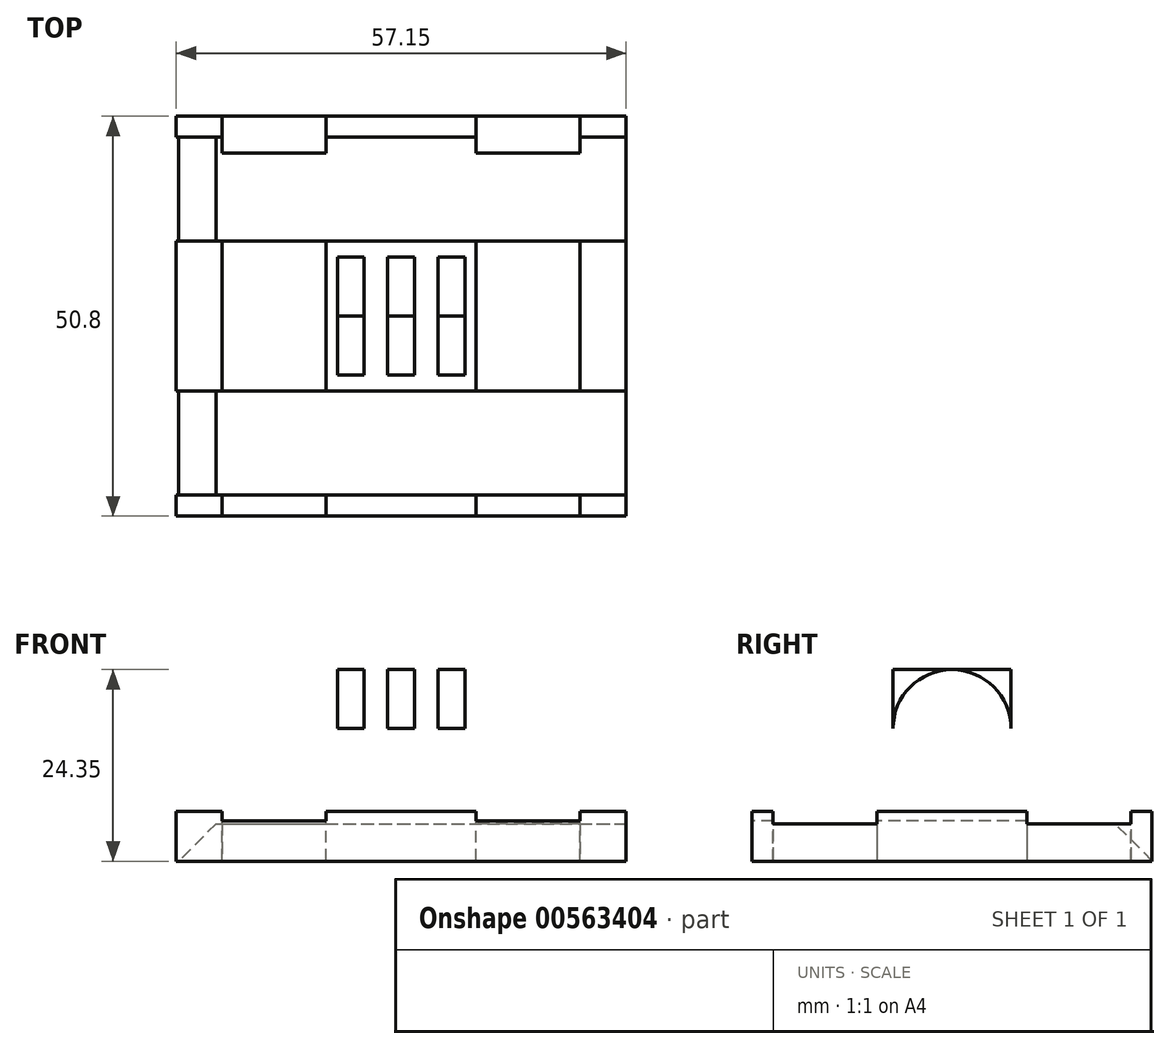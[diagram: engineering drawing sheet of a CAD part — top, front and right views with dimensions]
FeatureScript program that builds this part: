
annotation { "Feature Type Name" : "Feature", "Feature Type Description" : "" }
export const myFeature = defineFeature(function(context is Context, id is Id, definition is map)
    precondition{}
    {
        {
            var Q0;
            Q0=qCreatedBy(makeId("Top.planeOp"),FACE);
            var sketch = newSketch(context, id + "F0", { "sketchPlane" : qUnion([Q0])});
            skLineSegment(sketch, "E0.bottom", {"start": v(-28.58, 25.4) * mm, "end": v(28.58, 25.4) * mm});
            skLineSegment(sketch, "E0.top", {"start": v(-28.58, -25.4) * mm, "end": v(28.58, -25.4) * mm});
            skLineSegment(sketch, "E0.left", {"start": v(-28.57, 25.4) * mm, "end": v(-28.58, -25.4) * mm});
            skLineSegment(sketch, "E0.right", {"start": v(28.58, 25.4) * mm, "end": v(28.57, -25.4) * mm});
            skPoint(sketch, "E0.middle", {"position": v(0, 0) * mm});
            skSolve(sketch);
        }
        {
            var Q0;
            Q0=makeQuery(id+"F0.imprint","IMPRINT",FACE,{"disambiguationData":[TD([[makeQuery(id+"F0.imprint","IMPRINT",EDGE,{"derivedFrom":sQuery(id+"F0.wireOp",EDGE,"E0.bottom")}),-1.0]])]});
            extrude(context, id + "F1", {"entities" : qUnion([Q0]), "depth" : 6.35 * mm, "offsetDistance" : 25.4 * mm});
        }
        {
            var Q0;
            Q0=makeQuery(id+"FtcuCWjjDslHPHS_1.boolean.opBoolean","MERGE",FACE,{"derivedFrom":[makeQuery(id+"F1.opExtrude","SWEPT_FACE",FACE,{"disambiguationData":[OSD([sQuery(id+"F0.wireOp",EDGE,"E0.top")])]}),makeQuery(id+"FtcuCWjjDslHPHS_1.opExtrude","SWEPT_FACE",FACE,{"disambiguationData":[OSD([sQuery(id+"FMVw0hR87RWjdVx_1.wireOp",EDGE,"ffXjeifS-v08F-Zf74-KwMz-o1rhuZgXpIRW.top")])]}),makeQuery(id+"FtcuCWjjDslHPHS_1.opExtrude","SWEPT_FACE",FACE,{"disambiguationData":[OSD([sQuery(id+"FMVw0hR87RWjdVx_1.wireOp",EDGE,"9689fe90-bb07-47c0-8046-fc975a32ab120.MirrorCS")])]})]});
            var sketch = newSketch(context, id + "F2", { "sketchPlane" : qUnion([Q0])});
            skLineSegment(sketch, "E1.bottom", {"start": v(-22.73, 6.35) * mm, "end": v(-9.53, 6.35) * mm});
            skLineSegment(sketch, "E1.top", {"start": v(-22.73, 5.16) * mm, "end": v(-9.53, 5.16) * mm});
            skLineSegment(sketch, "E1.left", {"start": v(-22.73, 6.35) * mm, "end": v(-22.73, 5.16) * mm});
            skLineSegment(sketch, "E1.right", {"start": v(-9.53, 6.35) * mm, "end": v(-9.53, 5.16) * mm});
            skLineSegment(sketch, "E2.MirrorCS", {"start": v(9.53, 6.35) * mm, "end": v(9.53, 5.16) * mm});
            skLineSegment(sketch, "E3.MirrorCS", {"start": v(22.73, 6.35) * mm, "end": v(9.53, 6.35) * mm});
            skLineSegment(sketch, "E4.MirrorCS", {"start": v(22.73, 6.35) * mm, "end": v(22.73, 5.16) * mm});
            skLineSegment(sketch, "E5.MirrorCS", {"start": v(22.73, 5.16) * mm, "end": v(9.53, 5.16) * mm});
            skSolve(sketch);
        }
        {
            var Q0;
            Q0=qSketchRegion(id+"F2",true);
            extrude(context, id + "F3", {"entities" : qUnion([Q0]), "operationType" : NewBodyOperationType.REMOVE, "endBound" : BoundingType.THROUGH_ALL, "oppositeDirection" : true, "depth" : 25.4 * mm, "offsetDistance" : 25.4 * mm});
        }
        {
            var Q0;
            Q0=makeQuery(id+"F3.boolean.opBoolean","COPY",EDGE,{"derivedFrom":makeQuery(id+"F3.opExtrude","CAP_EDGE",EDGE,{"disambiguationData":[OSD([sQuery(id+"F2.wireOp",EDGE,"E1.top")])],"isStart":true})});
            var Q1;
            Q1=makeQuery(id+"F3.boolean.opBoolean","INTERSECT",EDGE,{"derivedFrom":[makeQuery(id+"FtcuCWjjDslHPHS_1.boolean.opBoolean","MERGE",FACE,{"derivedFrom":[makeQuery(id+"F1.opExtrude","SWEPT_FACE",FACE,{"disambiguationData":[OSD([sQuery(id+"F0.wireOp",EDGE,"E0.bottom")])]}),makeQuery(id+"FtcuCWjjDslHPHS_1.opExtrude","SWEPT_FACE",FACE,{"disambiguationData":[OSD([sQuery(id+"FMVw0hR87RWjdVx_1.wireOp",EDGE,"ffXjeifS-v08F-Zf74-KwMz-o1rhuZgXpIRW.bottom")])]}),makeQuery(id+"FtcuCWjjDslHPHS_1.opExtrude","SWEPT_FACE",FACE,{"disambiguationData":[OSD([sQuery(id+"FMVw0hR87RWjdVx_1.wireOp",EDGE,"d3afc862-6923-4452-8843-25e1cdd5f01b0.MirrorCS")])]})]}),makeQuery(id+"F3.opExtrude","SWEPT_FACE",FACE,{"disambiguationData":[OSD([sQuery(id+"F2.wireOp",EDGE,"E1.top")])]})]});
            var Q2;
            Q2=makeQuery(id+"F3.boolean.opBoolean","COPY",EDGE,{"derivedFrom":makeQuery(id+"F3.opExtrude","CAP_EDGE",EDGE,{"disambiguationData":[OSD([sQuery(id+"F2.wireOp",EDGE,"E5.MirrorCS")])],"isStart":true})});
            var Q3;
            Q3=makeQuery(id+"F3.boolean.opBoolean","INTERSECT",EDGE,{"derivedFrom":[makeQuery(id+"FtcuCWjjDslHPHS_1.boolean.opBoolean","MERGE",FACE,{"derivedFrom":[makeQuery(id+"F1.opExtrude","SWEPT_FACE",FACE,{"disambiguationData":[OSD([sQuery(id+"F0.wireOp",EDGE,"E0.bottom")])]}),makeQuery(id+"FtcuCWjjDslHPHS_1.opExtrude","SWEPT_FACE",FACE,{"disambiguationData":[OSD([sQuery(id+"FMVw0hR87RWjdVx_1.wireOp",EDGE,"ffXjeifS-v08F-Zf74-KwMz-o1rhuZgXpIRW.bottom")])]}),makeQuery(id+"FtcuCWjjDslHPHS_1.opExtrude","SWEPT_FACE",FACE,{"disambiguationData":[OSD([sQuery(id+"FMVw0hR87RWjdVx_1.wireOp",EDGE,"d3afc862-6923-4452-8843-25e1cdd5f01b0.MirrorCS")])]})]}),makeQuery(id+"F3.opExtrude","SWEPT_FACE",FACE,{"disambiguationData":[OSD([sQuery(id+"F2.wireOp",EDGE,"E5.MirrorCS")])]})]});
            chamfer(context, id + "F4", {"entities" : qUnion([Q0, Q1, Q2, Q3]), "width" : 5.08 * mm, "tangentPropagation" : true});
        }
        {
            var Q0;
            {var subQ0=sQuery(id+"F0.wireOp",EDGE,"E0.bottom");var subQ1=sQuery(id+"F0.wireOp",EDGE,"E0.top");Q0=makeQuery(id+"F3.boolean.opBoolean","SPLIT",FACE,{"disambiguationData":[TD([makeQuery(id+"F3.opExtrude","SWEPT_FACE",FACE,{"disambiguationData":[OSD([sQuery(id+"F2.wireOp",EDGE,"E1.right")])]})])],"derivedFrom":makeQuery(id+"F1.opExtrude","CAP_FACE",FACE,{"disambiguationData":[OSD([subQ0,subQ1,sQuery(id+"F0.wireOp",EDGE,"E0.left"),sQuery(id+"F0.wireOp",EDGE,"E0.right")])],"isStart":false})});}
            var sketch = newSketch(context, id + "F5", { "sketchPlane" : qUnion([Q0])});
            skLineSegment(sketch, "E6.bottom", {"start": v(-1.7, 7.5) * mm, "end": v(1.7, 7.5) * mm});
            skLineSegment(sketch, "E6.top", {"start": v(-1.7, -7.5) * mm, "end": v(1.7, -7.5) * mm});
            skLineSegment(sketch, "E6.left", {"start": v(-1.7, 7.5) * mm, "end": v(-1.7, -7.5) * mm});
            skLineSegment(sketch, "E6.right", {"start": v(1.7, 7.5) * mm, "end": v(1.7, -7.5) * mm});
            skPoint(sketch, "E6.middle", {"position": v(0, 0) * mm});
            skLineSegment(sketch, "E7.MirrorCS", {"start": v(1.7, 7.5) * mm, "end": v(-1.7, 7.5) * mm});
            skLineSegment(sketch, "E8.MirrorCS", {"start": v(1.7, -7.5) * mm, "end": v(-1.7, -7.5) * mm});
            skLineSegment(sketch, "E9.bottom", {"start": v(4.7, 7.5) * mm, "end": v(8.1, 7.5) * mm});
            skLineSegment(sketch, "E9.top", {"start": v(4.7, -7.5) * mm, "end": v(8.1, -7.5) * mm});
            skLineSegment(sketch, "E9.left", {"start": v(4.7, 7.5) * mm, "end": v(4.7, -7.5) * mm});
            skLineSegment(sketch, "E9.right", {"start": v(8.1, 7.5) * mm, "end": v(8.1, -7.5) * mm});
            skPoint(sketch, "E9.middle", {"position": v(6.4, 0) * mm});
            skLineSegment(sketch, "E10.bottom", {"start": v(-4.7, 7.5) * mm, "end": v(-8.1, 7.5) * mm});
            skLineSegment(sketch, "E10.top", {"start": v(-4.7, -7.5) * mm, "end": v(-8.1, -7.5) * mm});
            skLineSegment(sketch, "E10.left", {"start": v(-4.7, 7.5) * mm, "end": v(-4.7, -7.5) * mm});
            skLineSegment(sketch, "E10.right", {"start": v(-8.1, 7.5) * mm, "end": v(-8.1, -7.5) * mm});
            skPoint(sketch, "E10.middle", {"position": v(-6.4, 0) * mm});
            skSolve(sketch);
        }
        {
            var Q0;
            Q0=qSketchRegion(id+"F5",true);
            extrude(context, id + "F6", {"entities" : qUnion([Q0]), "operationType" : NewBodyOperationType.ADD, "depth" : 18 * mm, "offsetDistance" : 25.4 * mm});
        }
        {
            var Q0;
            Q0=makeQuery(id+"F1.opExtrude","SWEPT_FACE",FACE,{"disambiguationData":[OSD([sQuery(id+"F0.wireOp",EDGE,"E0.right")])]});
            var sketch = newSketch(context, id + "F7", { "sketchPlane" : qUnion([Q0])});
            skLineSegment(sketch, "E11.bottom", {"start": v(-22.73, 6.35) * mm, "end": v(-9.52, 6.35) * mm});
            skLineSegment(sketch, "E11.top", {"start": v(-22.73, 4.76) * mm, "end": v(-9.52, 4.76) * mm});
            skLineSegment(sketch, "E11.left", {"start": v(-22.73, 6.35) * mm, "end": v(-22.73, 4.76) * mm});
            skLineSegment(sketch, "E11.right", {"start": v(-9.52, 6.35) * mm, "end": v(-9.52, 4.76) * mm});
            skLineSegment(sketch, "E12.MirrorCS", {"start": v(9.53, 6.35) * mm, "end": v(9.53, 4.76) * mm});
            skLineSegment(sketch, "E13.MirrorCS", {"start": v(22.73, 6.35) * mm, "end": v(9.53, 6.35) * mm});
            skLineSegment(sketch, "E14.MirrorCS", {"start": v(22.73, 6.35) * mm, "end": v(22.73, 4.76) * mm});
            skLineSegment(sketch, "E15.MirrorCS", {"start": v(22.73, 4.76) * mm, "end": v(9.53, 4.76) * mm});
            skSolve(sketch);
        }
        {
            var Q0;
            Q0=qSketchRegion(id+"F7",true);
            extrude(context, id + "F8", {"entities" : qUnion([Q0]), "operationType" : NewBodyOperationType.REMOVE, "endBound" : BoundingType.THROUGH_ALL, "oppositeDirection" : true, "depth" : 25.4 * mm, "offsetDistance" : 25.4 * mm});
        }
        {
            var Q0;
            Q0=makeQuery(id+"F8.boolean.opBoolean","COPY",EDGE,{"derivedFrom":makeQuery(id+"F8.opExtrude","CAP_EDGE",EDGE,{"disambiguationData":[OSD([sQuery(id+"F7.wireOp",EDGE,"E15.MirrorCS")])],"isStart":true})});
            var Q1;
            Q1=makeQuery(id+"F8.boolean.opBoolean","COPY",EDGE,{"derivedFrom":makeQuery(id+"F8.opExtrude","CAP_EDGE",EDGE,{"disambiguationData":[OSD([sQuery(id+"F7.wireOp",EDGE,"E11.top")])],"isStart":true})});
            var Q2;
            Q2=makeQuery(id+"F8.boolean.opBoolean","INTERSECT",EDGE,{"derivedFrom":[makeQuery(id+"F1.opExtrude","SWEPT_FACE",FACE,{"disambiguationData":[OSD([sQuery(id+"F0.wireOp",EDGE,"E0.left")])]}),makeQuery(id+"F8.opExtrude","SWEPT_FACE",FACE,{"disambiguationData":[OSD([sQuery(id+"F7.wireOp",EDGE,"E15.MirrorCS")])]})]});
            var Q3;
            Q3=makeQuery(id+"F8.boolean.opBoolean","INTERSECT",EDGE,{"derivedFrom":[makeQuery(id+"F1.opExtrude","SWEPT_FACE",FACE,{"disambiguationData":[OSD([sQuery(id+"F0.wireOp",EDGE,"E0.left")])]}),makeQuery(id+"F8.opExtrude","SWEPT_FACE",FACE,{"disambiguationData":[OSD([sQuery(id+"F7.wireOp",EDGE,"E11.top")])]})]});
            chamfer(context, id + "F9", {"entities" : qUnion([Q0, Q1, Q2, Q3]), "width" : 5.08 * mm, "tangentPropagation" : true});
        }
        {
            var Q0;
            Q0=makeQuery(id+"F6.opExtrude","SWEPT_FACE",FACE,{"disambiguationData":[OSD([sQuery(id+"F5.wireOp",EDGE,"E9.right")])]});
            var sketch = newSketch(context, id + "F10", { "sketchPlane" : qUnion([Q0])});
            skPoint(sketch, "E16", {"position": v(0, 16.85) * mm});
            skArc(sketch, "E17", {"start": v(-7.5, 16.85) * mm, "mid": v(0, 24.35) * mm, "end": v(7.5, 16.85) * mm});
            skSolve(sketch);
        }
        {
            var Q0;
            Q0=sQuery(id+"F10.wireOp",VERTEX,"E16");
            var Q1;
            Q1=makeQuery(id+"F1.opExtrude","SWEPT_BODY",BODY,{"disambiguationData":[OSD([sQuery(id+"F0.wireOp",EDGE,"E0.bottom"),sQuery(id+"F0.wireOp",EDGE,"E0.top"),sQuery(id+"F0.wireOp",EDGE,"E0.left"),sQuery(id+"F0.wireOp",EDGE,"E0.right")])]});
            hole(context, id + "F11", {"style" : HoleStyle.SIMPLE, "endStyle" : HoleEndStyle.THROUGH, "holeDiameter" : 5 * mm, "isTappedThrough" : true, "tappedDepth" : 12.7 * mm, "tapClearance" : 3, "locations" : qUnion([Q0]), "scope" : qUnion([Q1])});
        }
        {
            var Q0;
            {var subQ0=sQuery(id+"F10.wireOp",EDGE,"E17");var subQ1=sQuery(id+"F5.wireOp",EDGE,"E9.right");var subQ4=makeQuery(id+"F6.opExtrude","CAP_EDGE",EDGE,{"disambiguationData":[OSD([subQ1])],"isStart":false});var subQ5=makeQuery(id+"F10.imprint","INTERSECT",VERTEX,{"derivedFrom":[subQ4,subQ0]});Q0=makeQuery(id+"F10.imprint","IMPRINT",FACE,{"disambiguationData":[TD([[makeQuery(id+"F10.imprint","IMPRINT",EDGE,{"disambiguationData":[TD([[subQ5,1.0]])],"derivedFrom":subQ0}),1.0]])]});}
            var Q1;
            {var subQ0=sQuery(id+"F10.wireOp",EDGE,"E17");var subQ1=sQuery(id+"F5.wireOp",EDGE,"E9.right");var subQ4=makeQuery(id+"F6.opExtrude","CAP_EDGE",EDGE,{"disambiguationData":[OSD([subQ1])],"isStart":false});var subQ5=makeQuery(id+"F10.imprint","INTERSECT",VERTEX,{"derivedFrom":[subQ4,subQ0]});Q1=makeQuery(id+"F10.imprint","IMPRINT",FACE,{"disambiguationData":[TD([[makeQuery(id+"F10.imprint","IMPRINT",EDGE,{"disambiguationData":[TD([[subQ5,-1.0]])],"derivedFrom":subQ0}),1.0]])]});}
            extrude(context, id + "F12", {"entities" : qUnion([Q0, Q1]), "operationType" : NewBodyOperationType.REMOVE, "endBound" : BoundingType.THROUGH_ALL, "oppositeDirection" : true, "depth" : 25.4 * mm, "offsetDistance" : 25.4 * mm});
        }
    });
